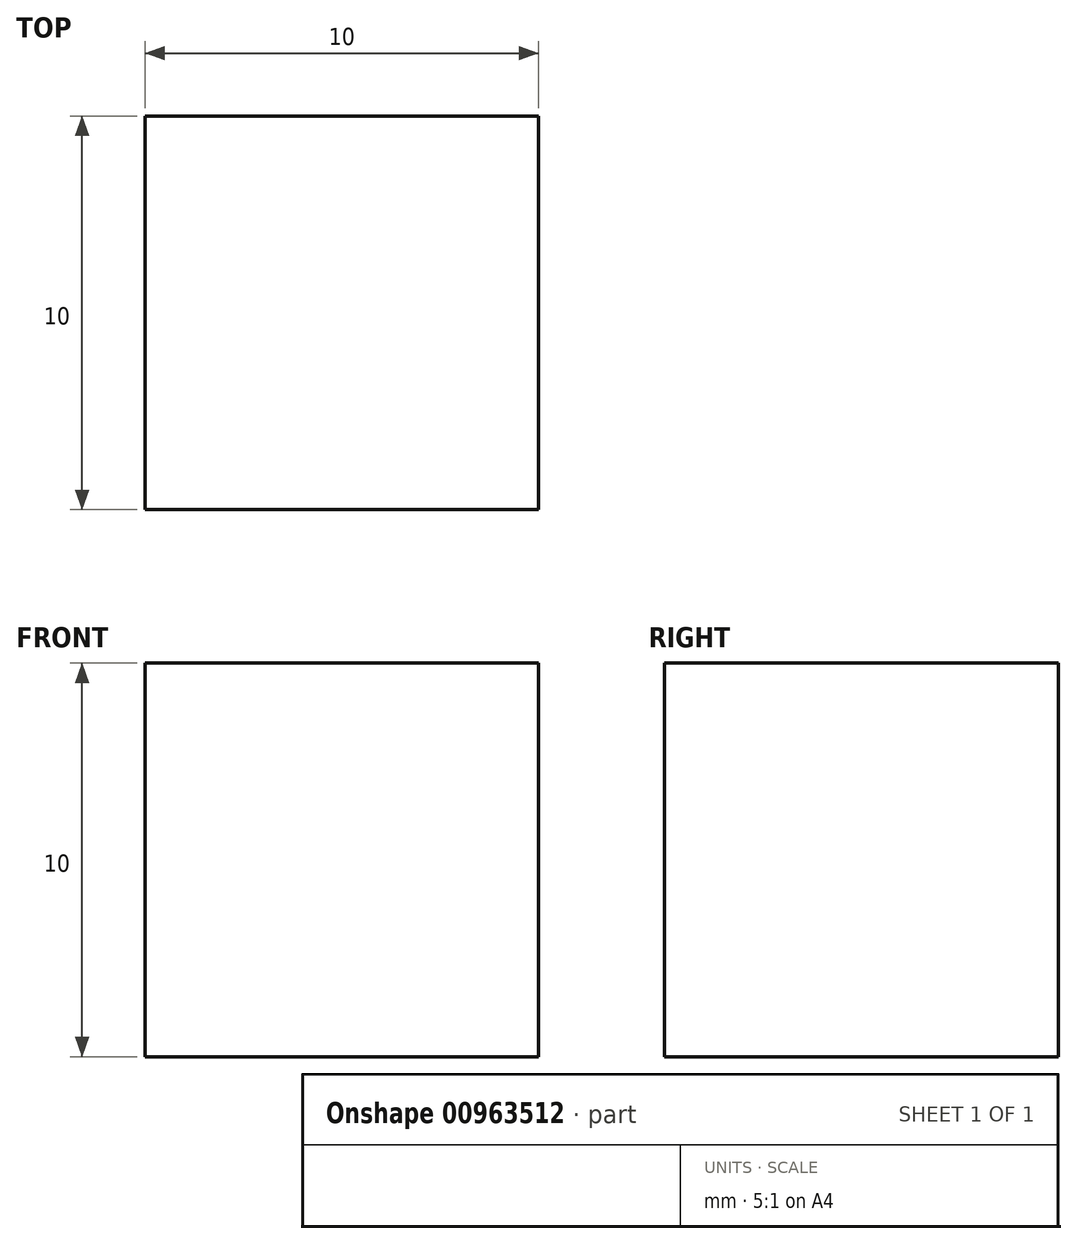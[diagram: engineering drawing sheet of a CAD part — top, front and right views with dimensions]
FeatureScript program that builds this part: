
annotation { "Feature Type Name" : "Feature", "Feature Type Description" : "" }
export const myFeature = defineFeature(function(context is Context, id is Id, definition is map)
    precondition{}
    {
        {
            var Q0;
            Q0=qCreatedBy(makeId("Front.planeOp"),FACE);
            var sketch = newSketch(context, id + "F0", { "sketchPlane" : qUnion([Q0])});
            skLineSegment(sketch, "E0.bottom", {"start": v(5, -5) * mm, "end": v(-5, -5) * mm});
            skLineSegment(sketch, "E0.top", {"start": v(5, 5) * mm, "end": v(-5, 5) * mm});
            skLineSegment(sketch, "E0.left", {"start": v(5, -5) * mm, "end": v(5, 5) * mm});
            skLineSegment(sketch, "E0.right", {"start": v(-5, -5) * mm, "end": v(-5, 5) * mm});
            skPoint(sketch, "E0.middle", {"position": v(0, 0) * mm});
            skSolve(sketch);
        }
        {
            var Q0;
            Q0=makeQuery(id+"F0.imprint","IMPRINT",FACE,{"disambiguationData":[TD([[makeQuery(id+"F0.imprint","IMPRINT",EDGE,{"derivedFrom":sQuery(id+"F0.wireOp",EDGE,"E0.bottom")}),-1.0]])]});
            extrude(context, id + "F1", {"entities" : qUnion([Q0]), "flatOperationType" : FlatOperationType.REMOVE, "depth" : 10 * mm, "offsetDistance" : 25 * mm, "domain" : OperationDomain.MODEL});
        }
    });
